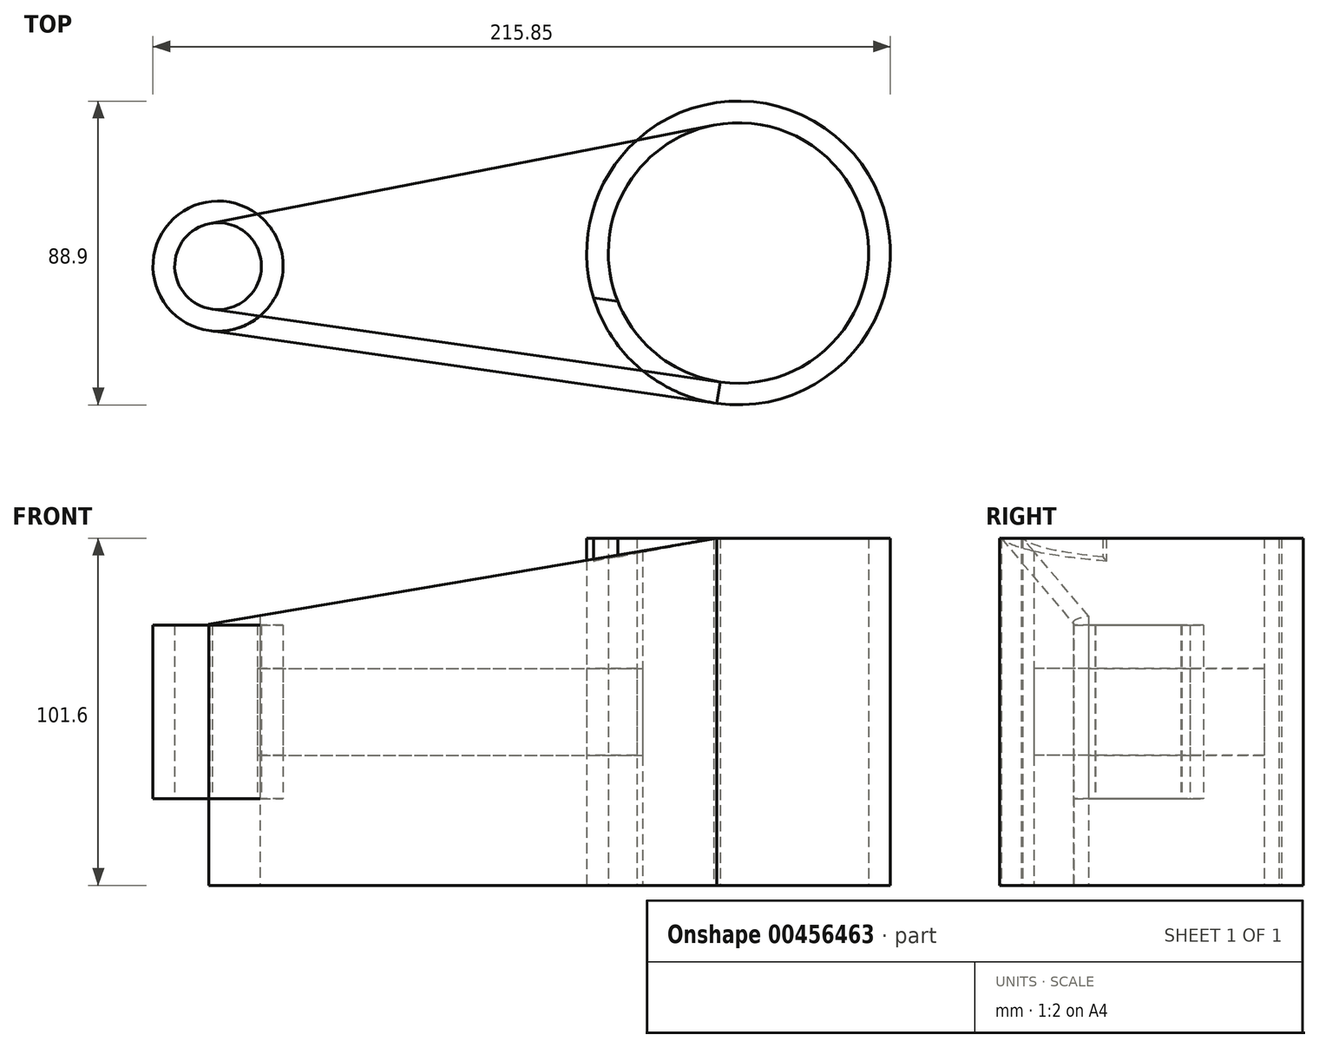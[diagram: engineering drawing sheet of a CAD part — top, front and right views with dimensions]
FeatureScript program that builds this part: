
annotation { "Feature Type Name" : "Feature", "Feature Type Description" : "" }
export const myFeature = defineFeature(function(context is Context, id is Id, definition is map)
    precondition{}
    {
        {
            var Q0;
            Q0=qCreatedBy(makeId("Top.planeOp"),FACE);
            var sketch = newSketch(context, id + "F0", { "sketchPlane" : qUnion([Q0])});
            skCircle(sketch, "E0", {"center": v(-72.47, 9.08) * mm, "radius": 19.05 * mm});
            skCircle(sketch, "E1", {"center": v(79.88, 12.94) * mm, "radius": 44.45 * mm});
            skLineSegment(sketch, "E2", {"start": v(-76.12, 27.78) * mm, "end": v(71.36, 56.56) * mm});
            skLineSegment(sketch, "E3", {"start": v(-75.17, -9.78) * mm, "end": v(73.58, -31.06) * mm});
            skCircle(sketch, "E4.0", {"center": v(79.88, 12.94) * mm, "radius": 38.1 * mm});
            skCircle(sketch, "E5.0", {"center": v(-72.47, 9.08) * mm, "radius": 12.7 * mm});
            skLineSegment(sketch, "E6", {"start": v(-72.47, 9.08) * mm, "end": v(79.88, 12.94) * mm, "construction": true});
            skLineSegment(sketch, "E7", {"start": v(-74.38, -3.48) * mm, "end": v(74.48, -24.78) * mm});
            skLineSegment(sketch, "E8", {"start": v(-74.9, 21.55) * mm, "end": v(72.58, 50.33) * mm});
            skSolve(sketch);
        }
        {
            var Q0;
            Q0=makeQuery(id+"F0.imprint","IMPRINT",FACE,{"disambiguationData":[TD([[makeQuery(id+"F0.imprint","IMPRINT",EDGE,{"derivedFrom":sQuery(id+"F0.wireOp",EDGE,"E5.0")}),-1.0]])]});
            extrude(context, id + "F1", {"entities" : qUnion([Q0]), "endBound" : BoundingType.SYMMETRIC, "depth" : 50.8 * mm});
        }
        {
            var Q0;
            {var subQ0=sQuery(id+"F0.wireOp",EDGE,"E8");var subQ1=sQuery(id+"F0.wireOp",EDGE,"E0");var subQ2=makeQuery(id+"F0.imprint","INTERSECT",VERTEX,{"derivedFrom":[subQ1,subQ0]});Q0=makeQuery(id+"F0.imprint","IMPRINT",FACE,{"disambiguationData":[TD([[makeQuery(id+"F0.imprint","IMPRINT",EDGE,{"disambiguationData":[TD([[subQ2,1.0]])],"derivedFrom":subQ1}),-1.0]])]});}
            extrude(context, id + "F2", {"entities" : qUnion([Q0]), "endBound" : BoundingType.SYMMETRIC, "depth" : 25.4 * mm});
        }
        {
            var Q0;
            {var subQ0=sQuery(id+"F0.wireOp",EDGE,"E1");var subQ1=makeQuery(id+"F0.imprint","INTERSECT",VERTEX,{"derivedFrom":[subQ0,sQuery(id+"F0.wireOp",EDGE,"E2")]});Q0=makeQuery(id+"F0.imprint","IMPRINT",FACE,{"disambiguationData":[TD([[makeQuery(id+"F0.imprint","IMPRINT",EDGE,{"disambiguationData":[TD([[subQ1,-1.0]])],"derivedFrom":subQ0}),1.0]])]});}
            extrude(context, id + "F3", {"entities" : qUnion([Q0]), "endBound" : BoundingType.SYMMETRIC, "depth" : 101.6 * mm});
        }
        {
            var Q0;
            {var subQ0=sQuery(id+"F0.wireOp",EDGE,"E8");var subQ1=sQuery(id+"F0.wireOp",EDGE,"E0");var subQ2=makeQuery(id+"F0.imprint","INTERSECT",VERTEX,{"derivedFrom":[subQ1,subQ0]});Q0=makeQuery(id+"F0.imprint","IMPRINT",FACE,{"disambiguationData":[TD([[makeQuery(id+"F0.imprint","IMPRINT",EDGE,{"disambiguationData":[TD([[subQ2,1.0]])],"derivedFrom":subQ1}),1.0]])]});}
            extrude(context, id + "F4", {"entities" : qUnion([Q0]), "endBound" : BoundingType.SYMMETRIC, "depth" : 50.8 * mm});
        }
        {
            var Q0;
            {var subQ0=sQuery(id+"F0.wireOp",EDGE,"E8");var subQ1=sQuery(id+"F0.wireOp",EDGE,"E1");var subQ2=makeQuery(id+"F0.imprint","INTERSECT",VERTEX,{"derivedFrom":[subQ1,subQ0]});Q0=makeQuery(id+"F0.imprint","IMPRINT",FACE,{"disambiguationData":[TD([[makeQuery(id+"F0.imprint","IMPRINT",EDGE,{"disambiguationData":[TD([[subQ2,-1.0]])],"derivedFrom":subQ1}),1.0]])]});}
            extrude(context, id + "F5", {"entities" : qUnion([Q0]), "endBound" : BoundingType.SYMMETRIC, "depth" : 101.6 * mm});
        }
        {
            var Q0;
            {var subQ0=sQuery(id+"F0.wireOp",EDGE,"E3");Q0=makeQuery(id+"F0.imprint","IMPRINT",FACE,{"disambiguationData":[TD([[makeQuery(id+"F0.imprint","IMPRINT",EDGE,{"derivedFrom":subQ0}),1.0]])]});}
            extrude(context, id + "F6", {"entities" : qUnion([Q0]), "endBound" : BoundingType.SYMMETRIC, "depth" : 101.6 * mm});
        }
        {
            var Q0;
            Q0=makeQuery(id+"F6.opExtrude","SWEPT_FACE",FACE,{"disambiguationData":[OSD([sQuery(id+"F0.wireOp",EDGE,"E3")])]});
            var sketch = newSketch(context, id + "F7", { "sketchPlane" : qUnion([Q0])});
            skLineSegment(sketch, "E9", {"start": v(77.24, 50.8) * mm, "end": v(-73.03, 25.65) * mm});
            skSolve(sketch);
        }
        {
            var Q0;
            Q0 = qSketchRegion(id + "F7", true);
            var Q1;
            {var subQ0=sQuery(id+"F7.wireOp",EDGE,"E9");Q1=makeQuery(id+"F7.imprint","IMPRINT",FACE,{"disambiguationData":[TD([[makeQuery(id+"F7.imprint","IMPRINT",EDGE,{"derivedFrom":subQ0}),-1.0]])]});}
            extrude(context, id + "F8", {"entities" : qUnion([Q0, Q1]), "operationType" : NewBodyOperationType.REMOVE, "oppositeDirection" : true, "depth" : 25.4 * mm});
        }
    });
